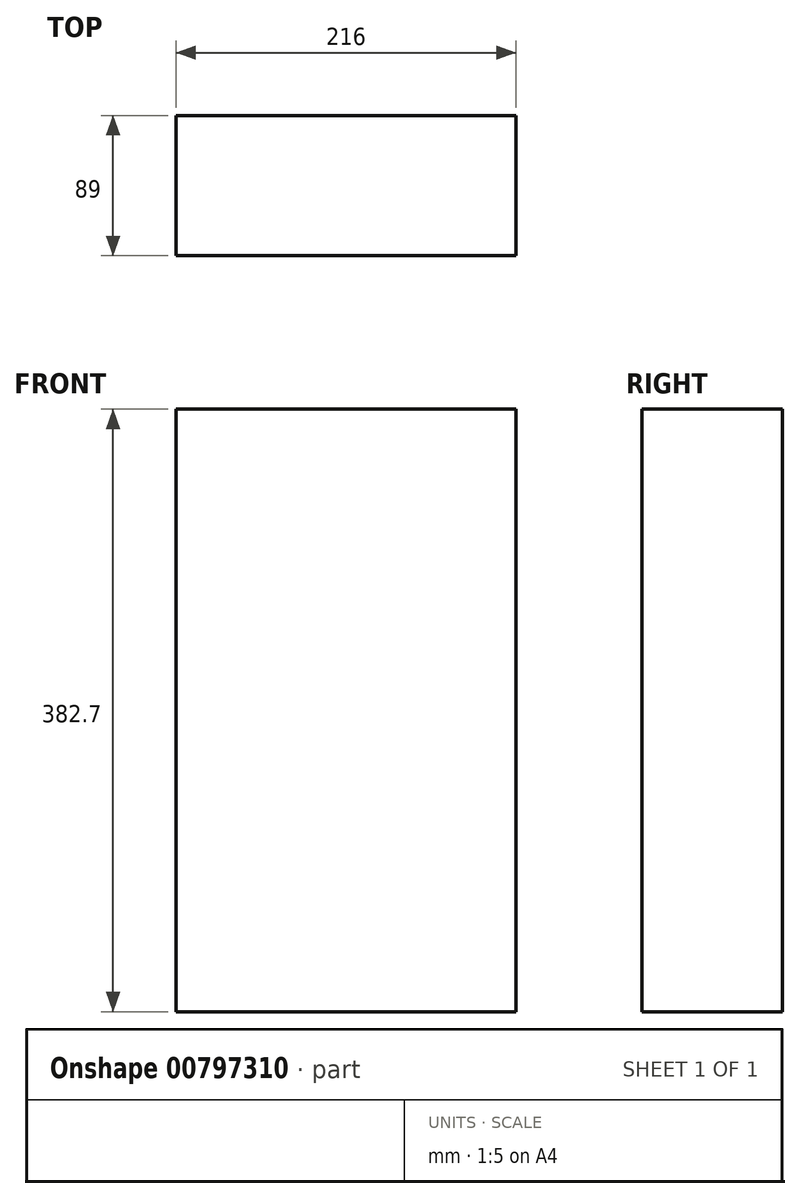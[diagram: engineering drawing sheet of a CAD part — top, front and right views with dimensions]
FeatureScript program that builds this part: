
annotation { "Feature Type Name" : "Feature", "Feature Type Description" : "" }
export const myFeature = defineFeature(function(context is Context, id is Id, definition is map)
    precondition{}
    {
        {
            var Q0;
            Q0=qCreatedBy(makeId("Front.planeOp"),FACE);
            var sketch = newSketch(context, id + "F0", { "sketchPlane" : qUnion([Q0])});
            skLineSegment(sketch, "E0.bottom", {"start": v(108, 191.35) * mm, "end": v(-108, 191.35) * mm});
            skLineSegment(sketch, "E0.top", {"start": v(108, -191.35) * mm, "end": v(-108, -191.35) * mm});
            skLineSegment(sketch, "E0.left", {"start": v(108, 191.35) * mm, "end": v(108, -191.35) * mm});
            skLineSegment(sketch, "E0.right", {"start": v(-108, 191.35) * mm, "end": v(-108, -191.35) * mm});
            skPoint(sketch, "E0.middle", {"position": v(0, 0) * mm});
            skSolve(sketch);
        }
        {
            var Q0;
            Q0=qSketchRegion(id+"F0",true);
            extrude(context, id + "F1", {"entities" : qUnion([Q0]), "depth" : 89 * mm, "offsetDistance" : 25 * mm, "symmetric" : true});
        }
    });
